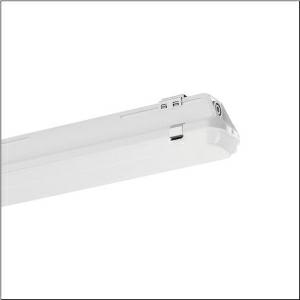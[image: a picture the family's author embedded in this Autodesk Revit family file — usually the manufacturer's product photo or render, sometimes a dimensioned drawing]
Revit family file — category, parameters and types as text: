
# Revit family: monsun_21_emergency_51fb107p437c3g
name_source: partatom
category: Lighting Fixtures
units: mm (PartAtom-declared; Revit-internal decimal feet)

## family parameters
Cut with Voids When Loaded = No
Host = Face
Light Source = No
Part Type = Normal
Room Calculation Point = No
Round Connector Dimension = Use Diameter
Shared = No

## types (1)
- --- (1 x LED, 910 lm, 7.1 W, 4000K)
    Apparent Load = 7 VA
    CIE Flux Codes = 47 77 93 94 100
    Color Rendering = 80
    Color Temperature = 4000K
    Default Elevation = 1800 mm
    Description = Monsun 21 emergency, damp-proof luminaire, chain hanger, primary optical cover: enclosure, of PMMA, light emission: direct distribution, primary light characteristic: symmetric, installation type: suspended mounting, surface-mounted, horizontal mounting, vertical mounting, LED, rated luminous flux: 3.860lm, luminous efficacy: 175lm/W, light colour: 840, colour temperature: 4000K, control gear: ON/OFF, with terminal, 4-pole, max. 2.5mm², mains connection: 220..240V, AC, 50/60Hz, rated input power: 26W, control gear: single battery element, battery: LiFePO4, 9Ah, housing, of glass-fibre reinforced polyester, uncoated, bright grey, incl. chain hanger, length: 1.590mm, width: 90mm, height: 88mm, clip for enclosure, of stainless steel (V2A), ceiling mounting element, of stainless steel (V2A), chain hanger, of stainless steel (V2A), protection rating (complete): IP66, insulation class (complete): insulation class I (protective earthing), certification: CE, UKCA, protection symbol: D, impact resistance: IK04, permissible operating ambient temperature: +5..+25°C, standard: EN 50419, EN 60598-2-1, EN 60598-2-22, corresponds to IFS (International Featured Standards) requirements for safety and quality in the food industry, for indoor or canopied outdoor use, no direct snow, no direct sun, no direct rain, LABS conformity tested according to VDMA 24364:2018-05, contact your sales advisor before using the luminaires in applications with unclear chemical exposure, large temperature fluctuations or condensation-forming humidity, packaging unit: 1 piece
    Height = 89 mm
    Lamp = 1 x LED
    Lamp Light Flux = 910 lm
    Lamp Power = 7.1 W
    Lamp count = 1
    Length = 1590 mm
    Luminous efficacy = 128 lm/W
    Manufacturer = Siteco
    ModVariant = No
    Model = 51FB107P437C3G
    Mounting Place = Ceiling
    Mounting Type = Surface mounted
    Number of Poles = 1
    OnlyDefault = Yes
    Power Factor = 1
    Product Name = Monsun 21 emergency
    Product group = damp-proof luminaire
    ProductGroupID = 300
    Protection Class = Protection class I
    Protection Degree = IP 66
    RLX_Detail_Level = 1
    RLX_Emergency_Light_Flux = 0 lm
    RLX_Emergency_Type = 0
    RLX_Emergency_Type_DB = No
    RlxData = <blob elided: 88733 chars, md5=f0b6d92d>
    Socket = socket
    Standby Power = 0 W
    System Light Flux = 910 lm
    System Power = 7 W
    Type Comments = : emergency light operation: 3 h
    Type Image = l_1319656.jpg
    URL = http://relux.com
    VarID = @adj_038377
    Voltage = 0 V
    Weight = 0.00 kg
    Width = 90 mm

## geometry (parser evidence)
native form markers: Blend x4, Sweep x12
no freeform markers — native parametric forms only
